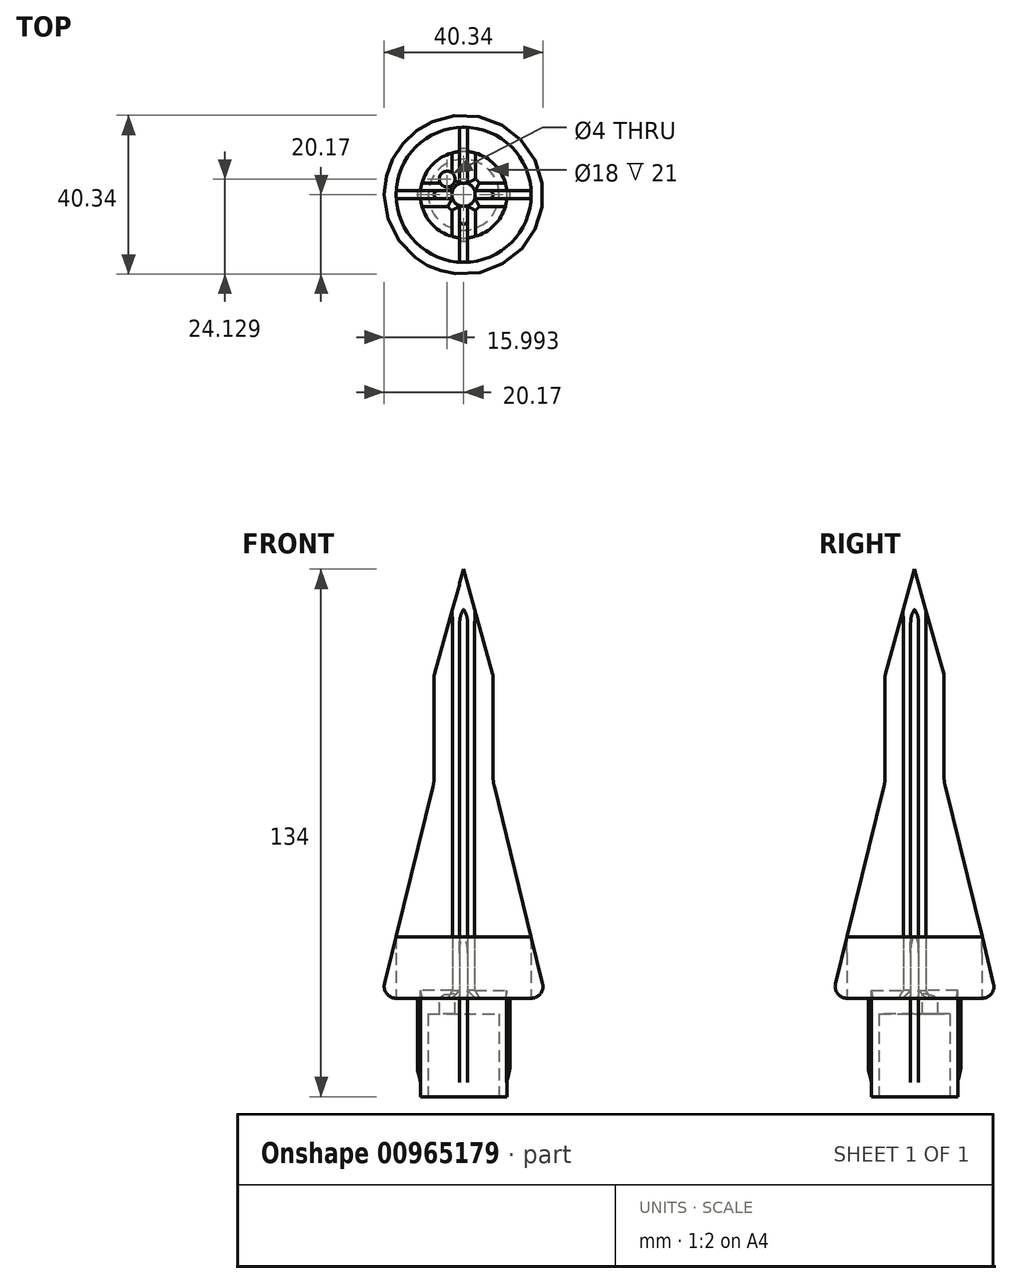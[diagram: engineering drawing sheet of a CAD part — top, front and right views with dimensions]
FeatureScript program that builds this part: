
annotation { "Feature Type Name" : "Feature", "Feature Type Description" : "" }
export const myFeature = defineFeature(function(context is Context, id is Id, definition is map)
    precondition{}
    {
        {
            var Q0;
            Q0=qCreatedBy(makeId("Right.planeOp"),FACE);
            var sketch = newSketch(context, id + "F0", { "sketchPlane" : qUnion([Q0])});
            skLineSegment(sketch, "E0", {"start": v(0, 0) * mm, "end": v(0, 134) * mm});
            skLineSegment(sketch, "E1", {"start": v(0, 134) * mm, "end": v(7.4, 107.4) * mm});
            skLineSegment(sketch, "E2", {"start": v(7.5, 106.6) * mm, "end": v(7.5, 81.2) * mm});
            skLineSegment(sketch, "E3", {"start": v(7.79, 78.83) * mm, "end": v(20.09, 28.72) * mm});
            skLineSegment(sketch, "E4", {"start": v(17.17, 25) * mm, "end": v(11.75, 25) * mm});
            skLineSegment(sketch, "E5", {"start": v(11.75, 25) * mm, "end": v(11.75, 7.37) * mm});
            skLineSegment(sketch, "E6", {"start": v(11.66, 6.64) * mm, "end": v(11.09, 4.36) * mm});
            skLineSegment(sketch, "E7", {"start": v(11, 3.63) * mm, "end": v(11, 0) * mm});
            skLineSegment(sketch, "E8", {"start": v(11, 0) * mm, "end": v(0, 0) * mm});
            skPoint(sketch, "E9.visualSharp", {"position": v(11.75, 25) * mm});
            skLineSegment(sketch, "E9.filletArc", {"start": v(11.75, 25) * mm, "end": v(11.75, 25) * mm});
            skPoint(sketch, "E10.visualSharp", {"position": v(21, 25) * mm});
            skArc(sketch, "E10.filletArc", {"start": v(17.17, 25) * mm, "mid": v(19.54, 26.15) * mm, "end": v(20.09, 28.72) * mm});
            skPoint(sketch, "E11.visualSharp", {"position": v(7.5, 80) * mm});
            skArc(sketch, "E11.filletArc", {"start": v(7.5, 81.2) * mm, "mid": v(7.57, 80) * mm, "end": v(7.79, 78.83) * mm});
            skPoint(sketch, "E12.visualSharp", {"position": v(7.5, 107) * mm});
            skArc(sketch, "E12.filletArc", {"start": v(7.5, 106.6) * mm, "mid": v(7.47, 107) * mm, "end": v(7.4, 107.4) * mm});
            skPoint(sketch, "E13.visualSharp", {"position": v(11.75, 7) * mm});
            skArc(sketch, "E13.filletArc", {"start": v(11.66, 6.64) * mm, "mid": v(11.73, 7) * mm, "end": v(11.75, 7.37) * mm});
            skPoint(sketch, "E14.visualSharp", {"position": v(11, 4) * mm});
            skArc(sketch, "E14.filletArc", {"start": v(11.09, 4.36) * mm, "mid": v(11.02, 4) * mm, "end": v(11, 3.63) * mm});
            skSolve(sketch);
        }
        {
            var Q0;
            Q0=makeQuery(id+"F0.imprint","IMPRINT",FACE,{"disambiguationData":[TD([[makeQuery(id+"F0.imprint","IMPRINT",EDGE,{"derivedFrom":sQuery(id+"F0.wireOp",EDGE,"E0")}),-1.0]])]});
            var Q1;
            Q1=sQuery(id+"F0.wireOp",EDGE,"E0");
            revolve(context, id + "F1", {"surfaceOperationType" : NewSurfaceOperationType.NEW, "entities" : qUnion([Q0]), "axis" : qUnion([Q1]), "revolveType" : RevolveType.FULL});
        }
        {
            var Q0;
            Q0=makeQuery(id+"F1.opRevolve","SWEPT_FACE",FACE,{"disambiguationData":[OSD([sQuery(id+"F0.wireOp",EDGE,"E4")])]});
            var sketch = newSketch(context, id + "F2", { "sketchPlane" : qUnion([Q0])});
            skCircle(sketch, "E15", {"center": v(0, 0) * mm, "radius": 3 * mm});
            skLineSegment(sketch, "E16", {"start": v(1, 22.83) * mm, "end": v(1, 2.83) * mm});
            skLineSegment(sketch, "E17", {"start": v(-2.83, 1) * mm, "end": v(22.83, 1) * mm});
            skArc(sketch, "E18", {"start": v(1, 22.83) * mm, "mid": v(16.16, 16.16) * mm, "end": v(22.83, 1) * mm});
            skLineSegment(sketch, "E19.1.0", {"start": v(-22.83, 1) * mm, "end": v(-2.83, 1) * mm});
            skArc(sketch, "E19.1.1", {"start": v(-22.83, 1) * mm, "mid": v(-16.16, 16.16) * mm, "end": v(-1, 22.83) * mm});
            skLineSegment(sketch, "E19.1.2", {"start": v(-1, -2.83) * mm, "end": v(-1, 22.83) * mm});
            skLineSegment(sketch, "E19.2.0", {"start": v(-1, -22.83) * mm, "end": v(-1, -2.83) * mm});
            skArc(sketch, "E19.2.1", {"start": v(-1, -22.83) * mm, "mid": v(-16.16, -16.16) * mm, "end": v(-22.83, -1) * mm});
            skLineSegment(sketch, "E19.2.2", {"start": v(2.83, -1) * mm, "end": v(-22.83, -1) * mm});
            skLineSegment(sketch, "E19.3.0", {"start": v(22.83, -1) * mm, "end": v(2.83, -1) * mm});
            skArc(sketch, "E19.3.1", {"start": v(22.83, -1) * mm, "mid": v(16.16, -16.16) * mm, "end": v(1, -22.83) * mm});
            skLineSegment(sketch, "E19.3.2", {"start": v(1, 2.83) * mm, "end": v(1, -22.83) * mm});
            skSolve(sketch);
        }
        {
            var Q0;
            {var subQ0=sQuery(id+"F2.wireOp",EDGE,"E18");Q0=makeQuery(id+"F2.imprint","IMPRINT",FACE,{"disambiguationData":[TD([[makeQuery(id+"F2.imprint","IMPRINT",EDGE,{"derivedFrom":subQ0}),-1.0]])]});}
            var Q1;
            {var subQ0=sQuery(id+"F2.wireOp",EDGE,"E16");var subQ1=sQuery(id+"F0.wireOp",EDGE,"E4");var subQ2=makeQuery(id+"F1.opRevolve","SWEPT_EDGE",EDGE,{"disambiguationData":[OSD([subQ1,sQuery(id+"F0.wireOp",EDGE,"E10.filletArc")])]});var subQ3=makeQuery(id+"F2.imprint","INTERSECT",VERTEX,{"derivedFrom":[subQ2,subQ0]});Q1=makeQuery(id+"F2.imprint","IMPRINT",FACE,{"disambiguationData":[TD([[makeQuery(id+"F2.imprint","IMPRINT",EDGE,{"disambiguationData":[TD([[subQ3,-1.0]])],"derivedFrom":subQ0}),1.0]])]});}
            var Q2;
            {var subQ0=sQuery(id+"F2.wireOp",EDGE,"E16");var subQ1=sQuery(id+"F2.wireOp",EDGE,"E15");var subQ2=makeQuery(id+"F2.imprint","INTERSECT",VERTEX,{"derivedFrom":[subQ1,subQ0]});Q2=makeQuery(id+"F2.imprint","IMPRINT",FACE,{"disambiguationData":[TD([[makeQuery(id+"F2.imprint","IMPRINT",EDGE,{"disambiguationData":[TD([[subQ2,1.0]])],"derivedFrom":subQ1}),-1.0]])]});}
            var Q3;
            {var subQ0=sQuery(id+"F2.wireOp",EDGE,"E19.1.0");var subQ1=sQuery(id+"F2.wireOp",EDGE,"E15");var subQ2=makeQuery(id+"F2.imprint","INTERSECT",VERTEX,{"derivedFrom":[subQ1,subQ0]});Q3=makeQuery(id+"F2.imprint","IMPRINT",FACE,{"disambiguationData":[TD([[makeQuery(id+"F2.imprint","IMPRINT",EDGE,{"disambiguationData":[TD([[subQ2,1.0]])],"derivedFrom":subQ1}),-1.0]])]});}
            var Q4;
            {var subQ0=sQuery(id+"F2.wireOp",EDGE,"E19.1.0");var subQ1=sQuery(id+"F0.wireOp",EDGE,"E4");var subQ2=makeQuery(id+"F1.opRevolve","SWEPT_EDGE",EDGE,{"disambiguationData":[OSD([subQ1,sQuery(id+"F0.wireOp",EDGE,"E10.filletArc")])]});var subQ3=makeQuery(id+"F2.imprint","INTERSECT",VERTEX,{"derivedFrom":[subQ2,subQ0]});Q4=makeQuery(id+"F2.imprint","IMPRINT",FACE,{"disambiguationData":[TD([[makeQuery(id+"F2.imprint","IMPRINT",EDGE,{"disambiguationData":[TD([[subQ3,-1.0]])],"derivedFrom":subQ0}),1.0]])]});}
            var Q5;
            {var subQ0=sQuery(id+"F2.wireOp",EDGE,"E19.1.1");Q5=makeQuery(id+"F2.imprint","IMPRINT",FACE,{"disambiguationData":[TD([[makeQuery(id+"F2.imprint","IMPRINT",EDGE,{"derivedFrom":subQ0}),-1.0]])]});}
            var Q6;
            {var subQ0=sQuery(id+"F2.wireOp",EDGE,"E19.3.1");Q6=makeQuery(id+"F2.imprint","IMPRINT",FACE,{"disambiguationData":[TD([[makeQuery(id+"F2.imprint","IMPRINT",EDGE,{"derivedFrom":subQ0}),-1.0]])]});}
            var Q7;
            {var subQ0=sQuery(id+"F2.wireOp",EDGE,"E19.3.0");var subQ1=sQuery(id+"F0.wireOp",EDGE,"E4");var subQ2=makeQuery(id+"F1.opRevolve","SWEPT_EDGE",EDGE,{"disambiguationData":[OSD([subQ1,sQuery(id+"F0.wireOp",EDGE,"E10.filletArc")])]});var subQ3=makeQuery(id+"F2.imprint","INTERSECT",VERTEX,{"derivedFrom":[subQ2,subQ0]});Q7=makeQuery(id+"F2.imprint","IMPRINT",FACE,{"disambiguationData":[TD([[makeQuery(id+"F2.imprint","IMPRINT",EDGE,{"disambiguationData":[TD([[subQ3,-1.0]])],"derivedFrom":subQ0}),1.0]])]});}
            var Q8;
            {var subQ0=sQuery(id+"F2.wireOp",EDGE,"E19.3.0");var subQ1=sQuery(id+"F2.wireOp",EDGE,"E15");var subQ2=makeQuery(id+"F2.imprint","INTERSECT",VERTEX,{"derivedFrom":[subQ1,subQ0]});Q8=makeQuery(id+"F2.imprint","IMPRINT",FACE,{"disambiguationData":[TD([[makeQuery(id+"F2.imprint","IMPRINT",EDGE,{"disambiguationData":[TD([[subQ2,1.0]])],"derivedFrom":subQ1}),-1.0]])]});}
            var Q9;
            {var subQ0=sQuery(id+"F2.wireOp",EDGE,"E19.2.1");Q9=makeQuery(id+"F2.imprint","IMPRINT",FACE,{"disambiguationData":[TD([[makeQuery(id+"F2.imprint","IMPRINT",EDGE,{"derivedFrom":subQ0}),-1.0]])]});}
            var Q10;
            {var subQ0=sQuery(id+"F2.wireOp",EDGE,"E19.2.0");var subQ1=sQuery(id+"F0.wireOp",EDGE,"E4");var subQ2=makeQuery(id+"F1.opRevolve","SWEPT_EDGE",EDGE,{"disambiguationData":[OSD([subQ1,sQuery(id+"F0.wireOp",EDGE,"E10.filletArc")])]});var subQ3=makeQuery(id+"F2.imprint","INTERSECT",VERTEX,{"derivedFrom":[subQ2,subQ0]});Q10=makeQuery(id+"F2.imprint","IMPRINT",FACE,{"disambiguationData":[TD([[makeQuery(id+"F2.imprint","IMPRINT",EDGE,{"disambiguationData":[TD([[subQ3,-1.0]])],"derivedFrom":subQ0}),1.0]])]});}
            var Q11;
            {var subQ0=sQuery(id+"F2.wireOp",EDGE,"E19.2.0");var subQ1=sQuery(id+"F2.wireOp",EDGE,"E15");var subQ2=makeQuery(id+"F2.imprint","INTERSECT",VERTEX,{"derivedFrom":[subQ1,subQ0]});Q11=makeQuery(id+"F2.imprint","IMPRINT",FACE,{"disambiguationData":[TD([[makeQuery(id+"F2.imprint","IMPRINT",EDGE,{"disambiguationData":[TD([[subQ2,1.0]])],"derivedFrom":subQ1}),-1.0]])]});}
            extrude(context, id + "F3", {"entities" : qUnion([Q0, Q1, Q2, Q3, Q4, Q5, Q6, Q7, Q8, Q9, Q10, Q11]), "operationType" : NewBodyOperationType.REMOVE, "oppositeDirection" : true, "depth" : 150 * mm, "offsetDistance" : 25 * mm});
        }
        {
            var Q0;
            Q0=makeQuery(id+"F3.boolean.opBoolean","COPY",FACE,{"derivedFrom":makeQuery(id+"F3.opExtrude","CAP_FACE",FACE,{"disambiguationData":[OSD([sQuery(id+"F2.wireOp",EDGE,"E15"),sQuery(id+"F2.wireOp",EDGE,"E19.2.0"),sQuery(id+"F2.wireOp",EDGE,"E19.2.1"),sQuery(id+"F2.wireOp",EDGE,"E19.2.2")])],"isStart":true})});
            var sketch = newSketch(context, id + "F4", { "sketchPlane" : qUnion([Q0])});
            skCircle(sketch, "E20", {"center": v(0, 0) * mm, "radius": 11 * mm});
            skLineSegment(sketch, "E21", {"start": v(-10.95, 1) * mm, "end": v(-15.95, 1) * mm});
            skLineSegment(sketch, "E22", {"start": v(-1, 10.95) * mm, "end": v(-1, 15.95) * mm});
            skArc(sketch, "E23", {"start": v(-15.95, 1) * mm, "mid": v(-11.3, 11.3) * mm, "end": v(-1, 15.95) * mm});
            skLineSegment(sketch, "E24.1.0", {"start": v(-10.95, -1) * mm, "end": v(-15.95, -1) * mm});
            skArc(sketch, "E24.1.1", {"start": v(-1, -15.95) * mm, "mid": v(-11.3, -11.3) * mm, "end": v(-15.95, -1) * mm});
            skLineSegment(sketch, "E24.1.2", {"start": v(-1, -10.95) * mm, "end": v(-1, -15.95) * mm});
            skLineSegment(sketch, "E24.2.0", {"start": v(1, -10.95) * mm, "end": v(1, -15.95) * mm});
            skArc(sketch, "E24.2.1", {"start": v(15.95, -1) * mm, "mid": v(11.3, -11.3) * mm, "end": v(1, -15.95) * mm});
            skLineSegment(sketch, "E24.2.2", {"start": v(10.95, -1) * mm, "end": v(15.95, -1) * mm});
            skLineSegment(sketch, "E24.3.0", {"start": v(10.95, 1) * mm, "end": v(15.95, 1) * mm});
            skArc(sketch, "E24.3.1", {"start": v(1, 15.95) * mm, "mid": v(11.3, 11.3) * mm, "end": v(15.95, 1) * mm});
            skLineSegment(sketch, "E24.3.2", {"start": v(1, 10.95) * mm, "end": v(1, 15.95) * mm});
            skCircle(sketch, "E25", {"center": v(-4.18, 3.96) * mm, "radius": 2 * mm});
            skSolve(sketch);
        }
        {
            var Q0;
            {var subQ1=sQuery(id+"F4.wireOp",EDGE,"E21");Q0=makeQuery(id+"F4.imprint","IMPRINT",FACE,{"disambiguationData":[TD([[makeQuery(id+"F4.imprint","IMPRINT",EDGE,{"derivedFrom":subQ1}),-1.0]])]});}
            var Q1;
            {var subQ1=sQuery(id+"F2.wireOp",EDGE,"E19.2.2");var subQ2=sQuery(id+"F2.wireOp",EDGE,"E19.2.0");var subQ3=makeQuery(id+"F3.opExtrude","CAP_FACE",FACE,{"disambiguationData":[OSD([sQuery(id+"F2.wireOp",EDGE,"E15"),subQ2,sQuery(id+"F2.wireOp",EDGE,"E19.2.1"),subQ1])],"isStart":true});var subQ8=sQuery(id+"F0.wireOp",EDGE,"E5");var subQ9=makeQuery(id+"F3.boolean.opBoolean","SPLIT",EDGE,{"disambiguationData":[topologyDisambiguationEdgeConnected([makeQuery(id+"F1.opRevolve","SWEPT_FACE",FACE,{"disambiguationData":[OSD([subQ8])]}),subQ3])],"derivedFrom":makeQuery(id+"F1.opRevolve","SWEPT_EDGE",EDGE,{"disambiguationData":[OSD([sQuery(id+"F0.wireOp",EDGE,"E4"),subQ8])]})});Q1=makeQuery(id+"F4.imprint","IMPRINT",FACE,{"disambiguationData":[TD([[makeQuery(id+"F4.imprint","IMPRINT",EDGE,{"derivedFrom":subQ9}),-1.0]])]});}
            var Q2;
            {var subQ0=sQuery(id+"F4.wireOp",EDGE,"E24.1.0");Q2=makeQuery(id+"F4.imprint","IMPRINT",FACE,{"disambiguationData":[TD([[makeQuery(id+"F4.imprint","IMPRINT",EDGE,{"derivedFrom":subQ0}),1.0]])]});}
            var Q3;
            {var subQ0=sQuery(id+"F4.wireOp",EDGE,"E24.2.0");Q3=makeQuery(id+"F4.imprint","IMPRINT",FACE,{"disambiguationData":[TD([[makeQuery(id+"F4.imprint","IMPRINT",EDGE,{"derivedFrom":subQ0}),1.0]])]});}
            var Q4;
            {var subQ0=sQuery(id+"F4.wireOp",EDGE,"E24.3.0");Q4=makeQuery(id+"F4.imprint","IMPRINT",FACE,{"disambiguationData":[TD([[makeQuery(id+"F4.imprint","IMPRINT",EDGE,{"derivedFrom":subQ0}),1.0]])]});}
            var Q5;
            {var subQ0=sQuery(id+"F4.wireOp",EDGE,"E25");var subQ1=sQuery(id+"F2.wireOp",EDGE,"E19.2.0");var subQ2=sQuery(id+"F2.wireOp",EDGE,"E15");var subQ4=makeQuery(id+"F3.boolean.opBoolean","COPY",EDGE,{"derivedFrom":makeQuery(id+"F3.opExtrude","CAP_EDGE",EDGE,{"disambiguationData":[OSD([subQ2]),TDD([makeQuery(id+"F2.imprint","IMPRINT",EDGE,{"disambiguationData":[TD([[makeQuery(id+"F2.imprint","INTERSECT",VERTEX,{"derivedFrom":[subQ2,subQ1]}),1.0]])],"derivedFrom":subQ2})])],"isStart":true})});var subQ5=makeQuery(id+"F4.imprint","INTERSECT",VERTEX,{"derivedFrom":[subQ4,subQ0]});Q5=makeQuery(id+"F4.imprint","IMPRINT",FACE,{"disambiguationData":[TD([[makeQuery(id+"F4.imprint","IMPRINT",EDGE,{"disambiguationData":[TD([[subQ5,-1.0]])],"derivedFrom":subQ0}),1.0]])]});}
            extrude(context, id + "F5", {"entities" : qUnion([Q0, Q1, Q2, Q3, Q4, Q5]), "operationType" : NewBodyOperationType.REMOVE, "oppositeDirection" : true, "depth" : 30 * mm, "offsetDistance" : 25 * mm});
        }
        {
            var Q0;
            Q0=makeQuery(id+"F1.opRevolve","SWEPT_FACE",FACE,{"disambiguationData":[OSD([sQuery(id+"F0.wireOp",EDGE,"E8")])]});
            var sketch = newSketch(context, id + "F6", { "sketchPlane" : qUnion([Q0])});
            skCircle(sketch, "E26", {"center": v(0, 0) * mm, "radius": 9 * mm});
            skSolve(sketch);
        }
        {
            var Q0;
            Q0=makeQuery(id+"F6.imprint","IMPRINT",FACE,{"disambiguationData":[TD([[makeQuery(id+"F6.imprint","IMPRINT",EDGE,{"derivedFrom":sQuery(id+"F6.wireOp",EDGE,"E26")}),1.0]])]});
            extrude(context, id + "F7", {"entities" : qUnion([Q0]), "operationType" : NewBodyOperationType.REMOVE, "oppositeDirection" : true, "depth" : 21 * mm, "offsetDistance" : 25 * mm});
        }
        {
            var Q0;
            {var subQ0=sQuery(id+"F2.wireOp",EDGE,"E19.3.0");Q0=makeQuery(id+"F3.boolean.opBoolean","COPY",EDGE,{"disambiguationData":[topologyDisambiguationEdgeConnected([makeQuery(id+"F3.opExtrude","CAP_FACE",FACE,{"disambiguationData":[OSD([sQuery(id+"F2.wireOp",EDGE,"E15"),subQ0,sQuery(id+"F2.wireOp",EDGE,"E19.3.1"),sQuery(id+"F2.wireOp",EDGE,"E19.3.2")])],"isStart":true})])],"derivedFrom":makeQuery(id+"F3.opExtrude","CAP_EDGE",EDGE,{"disambiguationData":[OSD([subQ0])],"isStart":true})});}
            var Q1;
            {var subQ0=sQuery(id+"F2.wireOp",EDGE,"E15");Q1=makeQuery(id+"F3.boolean.opBoolean","COPY",EDGE,{"derivedFrom":makeQuery(id+"F3.opExtrude","CAP_EDGE",EDGE,{"disambiguationData":[OSD([subQ0]),TDD([makeQuery(id+"F2.imprint","IMPRINT",EDGE,{"disambiguationData":[TD([[makeQuery(id+"F2.imprint","INTERSECT",VERTEX,{"derivedFrom":[subQ0,sQuery(id+"F2.wireOp",EDGE,"E19.3.2")]}),-1.0]])],"derivedFrom":subQ0})])],"isStart":true})});}
            var Q2;
            {var subQ0=sQuery(id+"F2.wireOp",EDGE,"E19.3.2");Q2=makeQuery(id+"F3.boolean.opBoolean","COPY",EDGE,{"disambiguationData":[topologyDisambiguationEdgeConnected([makeQuery(id+"F3.opExtrude","CAP_FACE",FACE,{"disambiguationData":[OSD([sQuery(id+"F2.wireOp",EDGE,"E15"),sQuery(id+"F2.wireOp",EDGE,"E19.3.0"),sQuery(id+"F2.wireOp",EDGE,"E19.3.1"),subQ0])],"isStart":true})])],"derivedFrom":makeQuery(id+"F3.opExtrude","CAP_EDGE",EDGE,{"disambiguationData":[OSD([subQ0])],"isStart":true})});}
            var Q3;
            {var subQ0=sQuery(id+"F2.wireOp",EDGE,"E15");Q3=makeQuery(id+"F3.boolean.opBoolean","COPY",EDGE,{"derivedFrom":makeQuery(id+"F3.opExtrude","CAP_EDGE",EDGE,{"disambiguationData":[OSD([subQ0]),TDD([makeQuery(id+"F2.imprint","IMPRINT",EDGE,{"disambiguationData":[TD([[makeQuery(id+"F2.imprint","INTERSECT",VERTEX,{"derivedFrom":[subQ0,sQuery(id+"F2.wireOp",EDGE,"E19.2.2")]}),-1.0]])],"derivedFrom":subQ0})])],"isStart":true})});}
            var Q4;
            {var subQ0=sQuery(id+"F2.wireOp",EDGE,"E19.2.2");Q4=makeQuery(id+"F3.boolean.opBoolean","COPY",EDGE,{"disambiguationData":[topologyDisambiguationEdgeConnected([makeQuery(id+"F3.opExtrude","CAP_FACE",FACE,{"disambiguationData":[OSD([sQuery(id+"F2.wireOp",EDGE,"E15"),sQuery(id+"F2.wireOp",EDGE,"E19.2.0"),sQuery(id+"F2.wireOp",EDGE,"E19.2.1"),subQ0])],"isStart":true})])],"derivedFrom":makeQuery(id+"F3.opExtrude","CAP_EDGE",EDGE,{"disambiguationData":[OSD([subQ0])],"isStart":true})});}
            var Q5;
            {var subQ0=sQuery(id+"F2.wireOp",EDGE,"E19.2.0");Q5=makeQuery(id+"F3.boolean.opBoolean","COPY",EDGE,{"disambiguationData":[topologyDisambiguationEdgeConnected([makeQuery(id+"F3.opExtrude","CAP_FACE",FACE,{"disambiguationData":[OSD([sQuery(id+"F2.wireOp",EDGE,"E15"),subQ0,sQuery(id+"F2.wireOp",EDGE,"E19.2.1"),sQuery(id+"F2.wireOp",EDGE,"E19.2.2")])],"isStart":true})])],"derivedFrom":makeQuery(id+"F3.opExtrude","CAP_EDGE",EDGE,{"disambiguationData":[OSD([subQ0])],"isStart":true})});}
            var Q6;
            {var subQ0=sQuery(id+"F2.wireOp",EDGE,"E19.1.2");Q6=makeQuery(id+"F3.boolean.opBoolean","COPY",EDGE,{"disambiguationData":[topologyDisambiguationEdgeConnected([makeQuery(id+"F3.opExtrude","CAP_FACE",FACE,{"disambiguationData":[OSD([sQuery(id+"F2.wireOp",EDGE,"E15"),sQuery(id+"F2.wireOp",EDGE,"E19.1.0"),sQuery(id+"F2.wireOp",EDGE,"E19.1.1"),subQ0])],"isStart":true})])],"derivedFrom":makeQuery(id+"F3.opExtrude","CAP_EDGE",EDGE,{"disambiguationData":[OSD([subQ0])],"isStart":true})});}
            var Q7;
            {var subQ0=sQuery(id+"F2.wireOp",EDGE,"E15");Q7=makeQuery(id+"F3.boolean.opBoolean","COPY",EDGE,{"derivedFrom":makeQuery(id+"F3.opExtrude","CAP_EDGE",EDGE,{"disambiguationData":[OSD([subQ0]),TDD([makeQuery(id+"F2.imprint","IMPRINT",EDGE,{"disambiguationData":[TD([[makeQuery(id+"F2.imprint","INTERSECT",VERTEX,{"derivedFrom":[subQ0,sQuery(id+"F2.wireOp",EDGE,"E19.1.2")]}),-1.0]])],"derivedFrom":subQ0})])],"isStart":true})});}
            var Q8;
            {var subQ0=sQuery(id+"F2.wireOp",EDGE,"E19.1.0");Q8=makeQuery(id+"F3.boolean.opBoolean","COPY",EDGE,{"disambiguationData":[topologyDisambiguationEdgeConnected([makeQuery(id+"F3.opExtrude","CAP_FACE",FACE,{"disambiguationData":[OSD([sQuery(id+"F2.wireOp",EDGE,"E15"),subQ0,sQuery(id+"F2.wireOp",EDGE,"E19.1.1"),sQuery(id+"F2.wireOp",EDGE,"E19.1.2")])],"isStart":true})])],"derivedFrom":makeQuery(id+"F3.opExtrude","CAP_EDGE",EDGE,{"disambiguationData":[OSD([subQ0])],"isStart":true})});}
            var Q9;
            {var subQ0=sQuery(id+"F2.wireOp",EDGE,"E17");Q9=makeQuery(id+"F3.boolean.opBoolean","COPY",EDGE,{"disambiguationData":[topologyDisambiguationEdgeConnected([makeQuery(id+"F3.opExtrude","CAP_FACE",FACE,{"disambiguationData":[OSD([sQuery(id+"F2.wireOp",EDGE,"E15"),sQuery(id+"F2.wireOp",EDGE,"E16"),subQ0,sQuery(id+"F2.wireOp",EDGE,"E18")])],"isStart":true})])],"derivedFrom":makeQuery(id+"F3.opExtrude","CAP_EDGE",EDGE,{"disambiguationData":[OSD([subQ0])],"isStart":true})});}
            var Q10;
            {var subQ0=sQuery(id+"F2.wireOp",EDGE,"E15");Q10=makeQuery(id+"F3.boolean.opBoolean","COPY",EDGE,{"derivedFrom":makeQuery(id+"F3.opExtrude","CAP_EDGE",EDGE,{"disambiguationData":[OSD([subQ0]),TDD([makeQuery(id+"F2.imprint","IMPRINT",EDGE,{"disambiguationData":[TD([[makeQuery(id+"F2.imprint","INTERSECT",VERTEX,{"derivedFrom":[subQ0,sQuery(id+"F2.wireOp",EDGE,"E17")]}),-1.0]])],"derivedFrom":subQ0})])],"isStart":true})});}
            var Q11;
            {var subQ0=sQuery(id+"F2.wireOp",EDGE,"E16");Q11=makeQuery(id+"F3.boolean.opBoolean","COPY",EDGE,{"disambiguationData":[topologyDisambiguationEdgeConnected([makeQuery(id+"F3.opExtrude","CAP_FACE",FACE,{"disambiguationData":[OSD([sQuery(id+"F2.wireOp",EDGE,"E15"),subQ0,sQuery(id+"F2.wireOp",EDGE,"E17"),sQuery(id+"F2.wireOp",EDGE,"E18")])],"isStart":true})])],"derivedFrom":makeQuery(id+"F3.opExtrude","CAP_EDGE",EDGE,{"disambiguationData":[OSD([subQ0])],"isStart":true})});}
            chamfer(context, id + "F8", {"entities" : qUnion([Q0, Q1, Q2, Q3, Q4, Q5, Q6, Q7, Q8, Q9, Q10, Q11]), "width" : 2 * mm, "tangentPropagation" : true});
        }
        {
            var Q0;
            {var subQ0=sQuery(id+"F2.wireOp",EDGE,"E15");Q0=makeQuery(id+"F3.boolean.opBoolean","INTERSECT",EDGE,{"derivedFrom":[makeQuery(id+"F1.opRevolve","SWEPT_FACE",FACE,{"disambiguationData":[OSD([sQuery(id+"F0.wireOp",EDGE,"E1")])]}),makeQuery(id+"F3.opExtrude","SWEPT_FACE",FACE,{"disambiguationData":[OSD([subQ0]),TDD([makeQuery(id+"F2.imprint","IMPRINT",EDGE,{"disambiguationData":[TD([[makeQuery(id+"F2.imprint","INTERSECT",VERTEX,{"derivedFrom":[subQ0,sQuery(id+"F2.wireOp",EDGE,"E19.3.2")]}),-1.0]])],"derivedFrom":subQ0})])]})]});}
            var Q1;
            {var subQ0=sQuery(id+"F2.wireOp",EDGE,"E15");Q1=makeQuery(id+"F3.boolean.opBoolean","INTERSECT",EDGE,{"derivedFrom":[makeQuery(id+"F1.opRevolve","SWEPT_FACE",FACE,{"disambiguationData":[OSD([sQuery(id+"F0.wireOp",EDGE,"E1")])]}),makeQuery(id+"F3.opExtrude","SWEPT_FACE",FACE,{"disambiguationData":[OSD([subQ0]),TDD([makeQuery(id+"F2.imprint","IMPRINT",EDGE,{"disambiguationData":[TD([[makeQuery(id+"F2.imprint","INTERSECT",VERTEX,{"derivedFrom":[subQ0,sQuery(id+"F2.wireOp",EDGE,"E19.2.2")]}),-1.0]])],"derivedFrom":subQ0})])]})]});}
            var Q2;
            {var subQ0=sQuery(id+"F2.wireOp",EDGE,"E15");Q2=makeQuery(id+"F3.boolean.opBoolean","INTERSECT",EDGE,{"derivedFrom":[makeQuery(id+"F1.opRevolve","SWEPT_FACE",FACE,{"disambiguationData":[OSD([sQuery(id+"F0.wireOp",EDGE,"E1")])]}),makeQuery(id+"F3.opExtrude","SWEPT_FACE",FACE,{"disambiguationData":[OSD([subQ0]),TDD([makeQuery(id+"F2.imprint","IMPRINT",EDGE,{"disambiguationData":[TD([[makeQuery(id+"F2.imprint","INTERSECT",VERTEX,{"derivedFrom":[subQ0,sQuery(id+"F2.wireOp",EDGE,"E19.1.2")]}),-1.0]])],"derivedFrom":subQ0})])]})]});}
            var Q3;
            {var subQ0=sQuery(id+"F2.wireOp",EDGE,"E15");Q3=makeQuery(id+"F3.boolean.opBoolean","INTERSECT",EDGE,{"derivedFrom":[makeQuery(id+"F1.opRevolve","SWEPT_FACE",FACE,{"disambiguationData":[OSD([sQuery(id+"F0.wireOp",EDGE,"E1")])]}),makeQuery(id+"F3.opExtrude","SWEPT_FACE",FACE,{"disambiguationData":[OSD([subQ0]),TDD([makeQuery(id+"F2.imprint","IMPRINT",EDGE,{"disambiguationData":[TD([[makeQuery(id+"F2.imprint","INTERSECT",VERTEX,{"derivedFrom":[subQ0,sQuery(id+"F2.wireOp",EDGE,"E17")]}),-1.0]])],"derivedFrom":subQ0})])]})]});}
            fillet(context, id + "F9", {"entities" : qUnion([Q0, Q1, Q2, Q3]), "radius" : 5 * mm, "tangentPropagation" : true, "allowEdgeOverflow" : false});
        }
        {
            var Q0;
            Q0=makeQuery(id+"F1.opRevolve","SWEPT_FACE",FACE,{"disambiguationData":[OSD([sQuery(id+"F0.wireOp",EDGE,"E1")])]});
            fillet(context, id + "F10", {"entities" : qUnion([Q0]), "radius" : 1 * mm, "tangentPropagation" : true, "allowEdgeOverflow" : false});
        }
    });
